# Revit family: Specialty_Equipment-Planter-Planters_Unlimited-Modern-Bristol Low Bowl Planter-rev
name_source: partatom
category: Specialty Equipment
units: mm (PartAtom-declared; Revit-internal decimal feet)

## family parameters
Always vertical = Yes
Cut with Voids When Loaded = No
Enable Cutting in Views = No
Maintain Annotation Orientation = No
OmniClass Number = 23.40.05.21.17
OmniClass Title = Planters
Part Type = Normal
Room Calculation Point = No
Round Connector Dimension = Use Diameter
Shared = No
Work Plane-Based = No

## types (3) — shared parameters
Assembly Code = G2050600
CD_Finish = Fiberglass
CD_Offset = 3 mm  [stored 0.00984252 ft]
CD_Product Page URL = https://www.plantersunlimited.com
CD_Specification = https://www.plantersunlimited.com
Description = Modular Planting Bed
Manufacturer = Planters Unlimited
Model = Modern Series Planters
Type Comments = Rocca Fiberglass Tapered Square Planter
URL = https://www.plantersunlimited.com
zero-valued in all types: Default Elevation

## per-type parameters (varying)
| type | CD_Height | CD_Stiffner | CD_Width | Distance |
| 40"Dia x 12H" | 305 mm | 152 mm | 1016 mm | 51 mm |
| 53"Dia x 16H" | 406 mm | 203 mm | 1346 mm | 68 mm |
| 27"Dia x 8H" | 203 mm | 102 mm | 686 mm | 34 mm |

note: [stored X ft] marks values corroborated as IEEE doubles in the binary element streams (Revit-internal decimal feet)

## geometry (parser evidence)
native form markers: Sweep x3
no freeform markers — native parametric forms only
